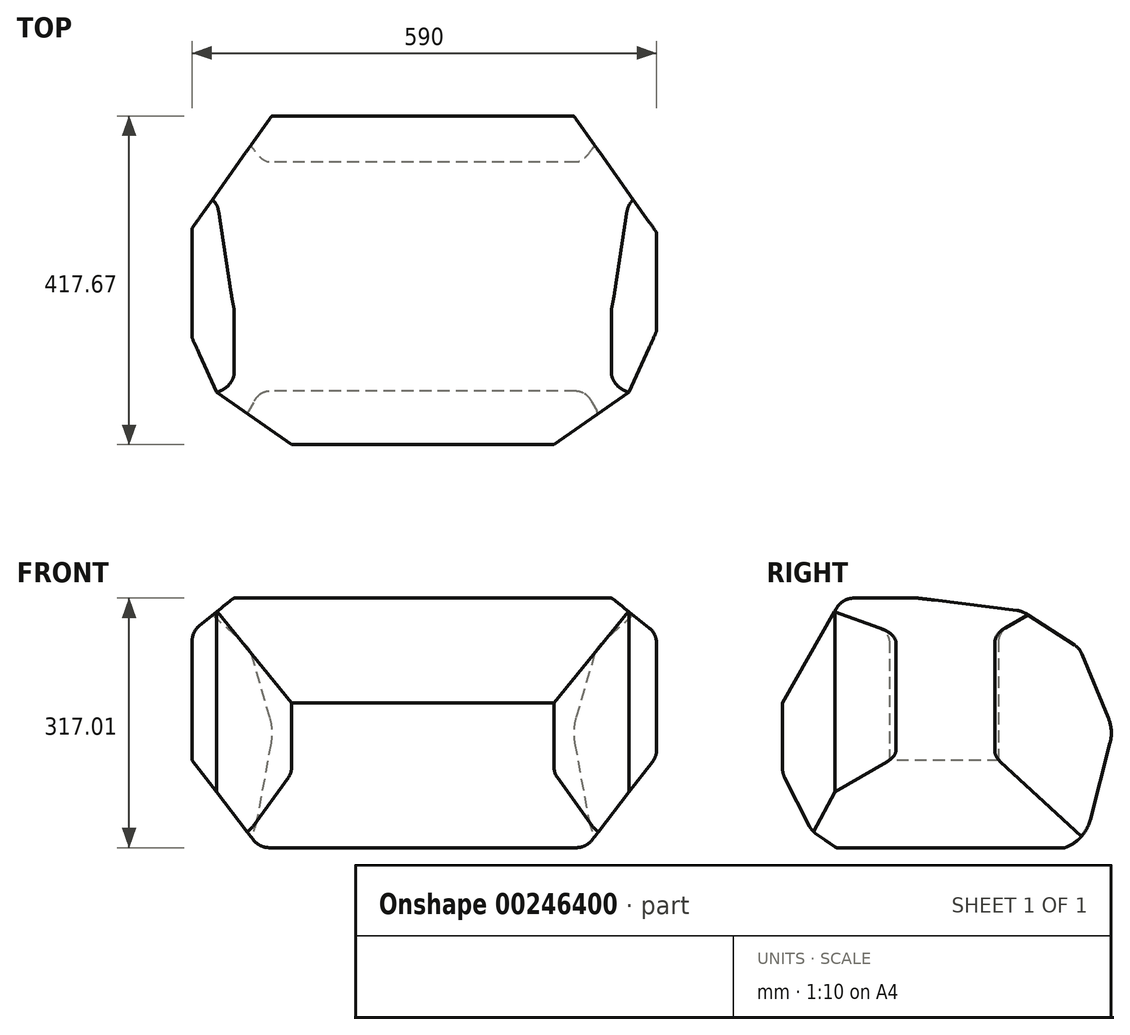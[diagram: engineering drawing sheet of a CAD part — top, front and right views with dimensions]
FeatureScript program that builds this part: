
annotation { "Feature Type Name" : "Feature", "Feature Type Description" : "" }
export const myFeature = defineFeature(function(context is Context, id is Id, definition is map)
    precondition{}
    {
        {
            var Q0;
            Q0=qCreatedBy(makeId("Front.planeOp"),FACE);
            var sketch = newSketch(context, id + "F0", { "sketchPlane" : qUnion([Q0])});
            skLineSegment(sketch, "E0", {"start": v(-293.04, 235.87) * mm, "end": v(296.96, 235.87) * mm, "construction": true});
            skLineSegment(sketch, "E1", {"start": v(0, 18.33) * mm, "end": v(0, 338.33) * mm, "construction": true});
            skLineSegment(sketch, "E2.bottom", {"start": v(-195, 18.33) * mm, "end": v(195, 18.33) * mm});
            skLineSegment(sketch, "E2.top", {"start": v(-227.65, 338.33) * mm, "end": v(227.65, 338.33) * mm});
            skLineSegment(sketch, "E2.left", {"start": v(-293.04, 18.33) * mm, "end": v(-293.04, 280.98) * mm});
            skLineSegment(sketch, "E2.right", {"start": v(296.96, 142.72) * mm, "end": v(296.96, 277.85) * mm});
            skLineSegment(sketch, "E3", {"start": v(215.08, 28.19) * mm, "end": v(291.65, 127.18) * mm});
            skLineSegment(sketch, "E4", {"start": v(287.41, 297.7) * mm, "end": v(243.5, 332.77) * mm});
            skLineSegment(sketch, "E5.MirrorCS", {"start": v(-283.5, 300.82) * mm, "end": v(-243.5, 332.77) * mm});
            skLineSegment(sketch, "E6.MirrorCS", {"start": v(-215.08, 28.19) * mm, "end": v(-293.04, 128.98) * mm});
            skPoint(sketch, "E7.orphan", {"position": v(-296.96, 290.07) * mm});
            skPoint(sketch, "E8.orphan", {"position": v(-296.96, 134.04) * mm});
            skPoint(sketch, "E9.newPointA", {"position": v(-207.46, 18.33) * mm});
            skPoint(sketch, "E9.newPointB", {"position": v(-293.04, 18.33) * mm});
            skArc(sketch, "E9.filletArc", {"start": v(-215.08, 28.19) * mm, "mid": v(-206.18, 20.92) * mm, "end": v(-195, 18.33) * mm});
            skPoint(sketch, "E10.newPointB", {"position": v(207.46, 18.33) * mm});
            skArc(sketch, "E10.filletArc", {"start": v(195, 18.33) * mm, "mid": v(206.18, 20.92) * mm, "end": v(215.08, 28.19) * mm});
            skPoint(sketch, "E11.newPointA", {"position": v(296.96, 134.04) * mm});
            skArc(sketch, "E11.filletArc", {"start": v(291.65, 127.18) * mm, "mid": v(295.6, 134.5) * mm, "end": v(296.96, 142.72) * mm});
            skPoint(sketch, "E12.newPointB", {"position": v(296.96, 290.07) * mm});
            skArc(sketch, "E12.filletArc", {"start": v(296.96, 277.85) * mm, "mid": v(294.45, 288.86) * mm, "end": v(287.41, 297.7) * mm});
            skPoint(sketch, "E13.newPointA", {"position": v(236.55, 338.33) * mm});
            skPoint(sketch, "E13.newPointB", {"position": v(296.96, 338.33) * mm});
            skArc(sketch, "E13.filletArc", {"start": v(243.5, 332.77) * mm, "mid": v(236.05, 336.9) * mm, "end": v(227.65, 338.33) * mm});
            skPoint(sketch, "E14.newPointB", {"position": v(-236.55, 338.33) * mm});
            skArc(sketch, "E14.filletArc", {"start": v(-227.65, 338.33) * mm, "mid": v(-236.05, 336.9) * mm, "end": v(-243.5, 332.77) * mm});
            skArc(sketch, "E15.filletArc", {"start": v(-283.5, 300.82) * mm, "mid": v(-290.53, 291.99) * mm, "end": v(-293.04, 280.98) * mm});
            skSolve(sketch);
        }
        {
            var Q0;
            Q0=qCreatedBy(makeId("Right.planeOp"),FACE);
            var sketch = newSketch(context, id + "F1", { "sketchPlane" : qUnion([Q0])});
            skLineSegment(sketch, "E16", {"start": v(122.6, 15.34) * mm, "end": v(122.6, 335.34) * mm, "construction": true});
            skLineSegment(sketch, "E17", {"start": v(122.6, 15.34) * mm, "end": v(341.6, 15.34) * mm});
            skLineSegment(sketch, "E18", {"start": v(390.78, 53.43) * mm, "end": v(416.05, 151.21) * mm});
            skLineSegment(sketch, "E19", {"start": v(413.82, 183.3) * mm, "end": v(380.43, 264.2) * mm});
            skLineSegment(sketch, "E20", {"start": v(370.69, 275.86) * mm, "end": v(308.22, 316.02) * mm});
            skLineSegment(sketch, "E21", {"start": v(297.6, 319.87) * mm, "end": v(173.55, 335.15) * mm});
            skLineSegment(sketch, "E22", {"start": v(170.44, 335.34) * mm, "end": v(122.6, 335.34) * mm});
            skLineSegment(sketch, "E23", {"start": v(68.61, 322.5) * mm, "end": v(0, 201.92) * mm});
            skLineSegment(sketch, "E24", {"start": v(0, 201.92) * mm, "end": v(0, 118.96) * mm});
            skLineSegment(sketch, "E25", {"start": v(2.75, 107.47) * mm, "end": v(34.22, 45.46) * mm});
            skLineSegment(sketch, "E26", {"start": v(42.42, 36.06) * mm, "end": v(65.87, 19.84) * mm});
            skLineSegment(sketch, "E27", {"start": v(80.32, 15.34) * mm, "end": v(122.6, 15.34) * mm});
            skLineSegment(sketch, "E28", {"start": v(90.69, 335.34) * mm, "end": v(122.6, 335.34) * mm});
            skPoint(sketch, "E29.visualSharp", {"position": v(75.92, 335.34) * mm});
            skArc(sketch, "E29.filletArc", {"start": v(90.69, 335.34) * mm, "mid": v(77.92, 331.9) * mm, "end": v(68.61, 322.5) * mm});
            skPoint(sketch, "E30.visualSharp", {"position": v(172, 335.34) * mm});
            skArc(sketch, "E30.filletArc", {"start": v(173.55, 335.15) * mm, "mid": v(172, 335.29) * mm, "end": v(170.44, 335.34) * mm});
            skPoint(sketch, "E31.visualSharp", {"position": v(303.35, 319.16) * mm});
            skArc(sketch, "E31.filletArc", {"start": v(308.22, 316.02) * mm, "mid": v(303.12, 318.54) * mm, "end": v(297.6, 319.87) * mm});
            skPoint(sketch, "E32.visualSharp", {"position": v(377.4, 271.55) * mm});
            skArc(sketch, "E32.filletArc", {"start": v(380.43, 264.2) * mm, "mid": v(376.46, 270.77) * mm, "end": v(370.69, 275.86) * mm});
            skPoint(sketch, "E33.visualSharp", {"position": v(0, 112.88) * mm});
            skArc(sketch, "E33.filletArc", {"start": v(0, 118.96) * mm, "mid": v(0.7, 113.05) * mm, "end": v(2.75, 107.47) * mm});
            skPoint(sketch, "E34.visualSharp", {"position": v(37.13, 39.72) * mm});
            skArc(sketch, "E34.filletArc", {"start": v(34.22, 45.46) * mm, "mid": v(37.73, 40.25) * mm, "end": v(42.42, 36.06) * mm});
            skPoint(sketch, "E35.visualSharp", {"position": v(72.4, 15.34) * mm});
            skArc(sketch, "E35.filletArc", {"start": v(65.87, 19.84) * mm, "mid": v(72.75, 16.49) * mm, "end": v(80.32, 15.34) * mm});
            skPoint(sketch, "E36.visualSharp", {"position": v(380.94, 15.34) * mm});
            skArc(sketch, "E36.filletArc", {"start": v(341.6, 15.34) * mm, "mid": v(372.7, 25.97) * mm, "end": v(390.78, 53.43) * mm});
            skPoint(sketch, "E37.visualSharp", {"position": v(420.3, 167.63) * mm});
            skArc(sketch, "E37.filletArc", {"start": v(416.05, 151.21) * mm, "mid": v(417.55, 167.44) * mm, "end": v(413.82, 183.3) * mm});
            skSolve(sketch);
        }
        {
            var Q0;
            Q0=makeQuery(id+"F0.imprint","IMPRINT",FACE,{"disambiguationData":[TD([[makeQuery(id+"F0.imprint","IMPRINT",EDGE,{"derivedFrom":sQuery(id+"F0.wireOp",EDGE,"E2.bottom")}),1.0]])]});
            extrude(context, id + "F2", {"entities" : qUnion([Q0]), "oppositeDirection" : true, "depth" : 431.8 * mm});
        }
        {
            var Q0;
            Q0 = qSketchRegion(id + "F1", true);
            extrude(context, id + "F3", {"entities" : qUnion([Q0]), "operationType" : NewBodyOperationType.INTERSECT, "depth" : 600 * mm, "symmetric" : true});
        }
        {
            var Q0;
            Q0=qCreatedBy(makeId("Top.planeOp"),FACE);
            var sketch = newSketch(context, id + "F4", { "sketchPlane" : qUnion([Q0])});
            skLineSegment(sketch, "E38", {"start": v(0, 0) * mm, "end": v(166.86, 0) * mm});
            skLineSegment(sketch, "E39", {"start": v(166.86, 0) * mm, "end": v(262.06, 66.6) * mm});
            skLineSegment(sketch, "E40", {"start": v(262.06, 66.6) * mm, "end": v(297.65, 145.78) * mm});
            skLineSegment(sketch, "E41", {"start": v(297.65, 145.78) * mm, "end": v(297.65, 268.56) * mm});
            skLineSegment(sketch, "E42", {"start": v(297.65, 268.56) * mm, "end": v(190.89, 418.91) * mm});
            skLineSegment(sketch, "E43", {"start": v(190.89, 418.91) * mm, "end": v(0, 418.91) * mm});
            skLineSegment(sketch, "E44.MirrorCS", {"start": v(-190.89, 418.91) * mm, "end": v(0, 418.91) * mm});
            skLineSegment(sketch, "E45.MirrorCS", {"start": v(-297.65, 268.56) * mm, "end": v(-190.89, 418.91) * mm});
            skLineSegment(sketch, "E46.MirrorCS", {"start": v(-297.65, 145.78) * mm, "end": v(-297.65, 268.56) * mm});
            skLineSegment(sketch, "E47.MirrorCS", {"start": v(-262.06, 66.6) * mm, "end": v(-297.65, 145.78) * mm});
            skLineSegment(sketch, "E48.MirrorCS", {"start": v(-166.86, 0) * mm, "end": v(-262.06, 66.6) * mm});
            skLineSegment(sketch, "E49.MirrorCS", {"start": v(0, 0) * mm, "end": v(-166.86, 0) * mm});
            skSolve(sketch);
        }
        {
            var Q0;
            Q0 = qSketchRegion(id + "F4", true);
            extrude(context, id + "F5", {"entities" : qUnion([Q0]), "operationType" : NewBodyOperationType.INTERSECT, "endBound" : BoundingType.THROUGH_ALL, "depth" : 304.8 * mm});
        }
    });
